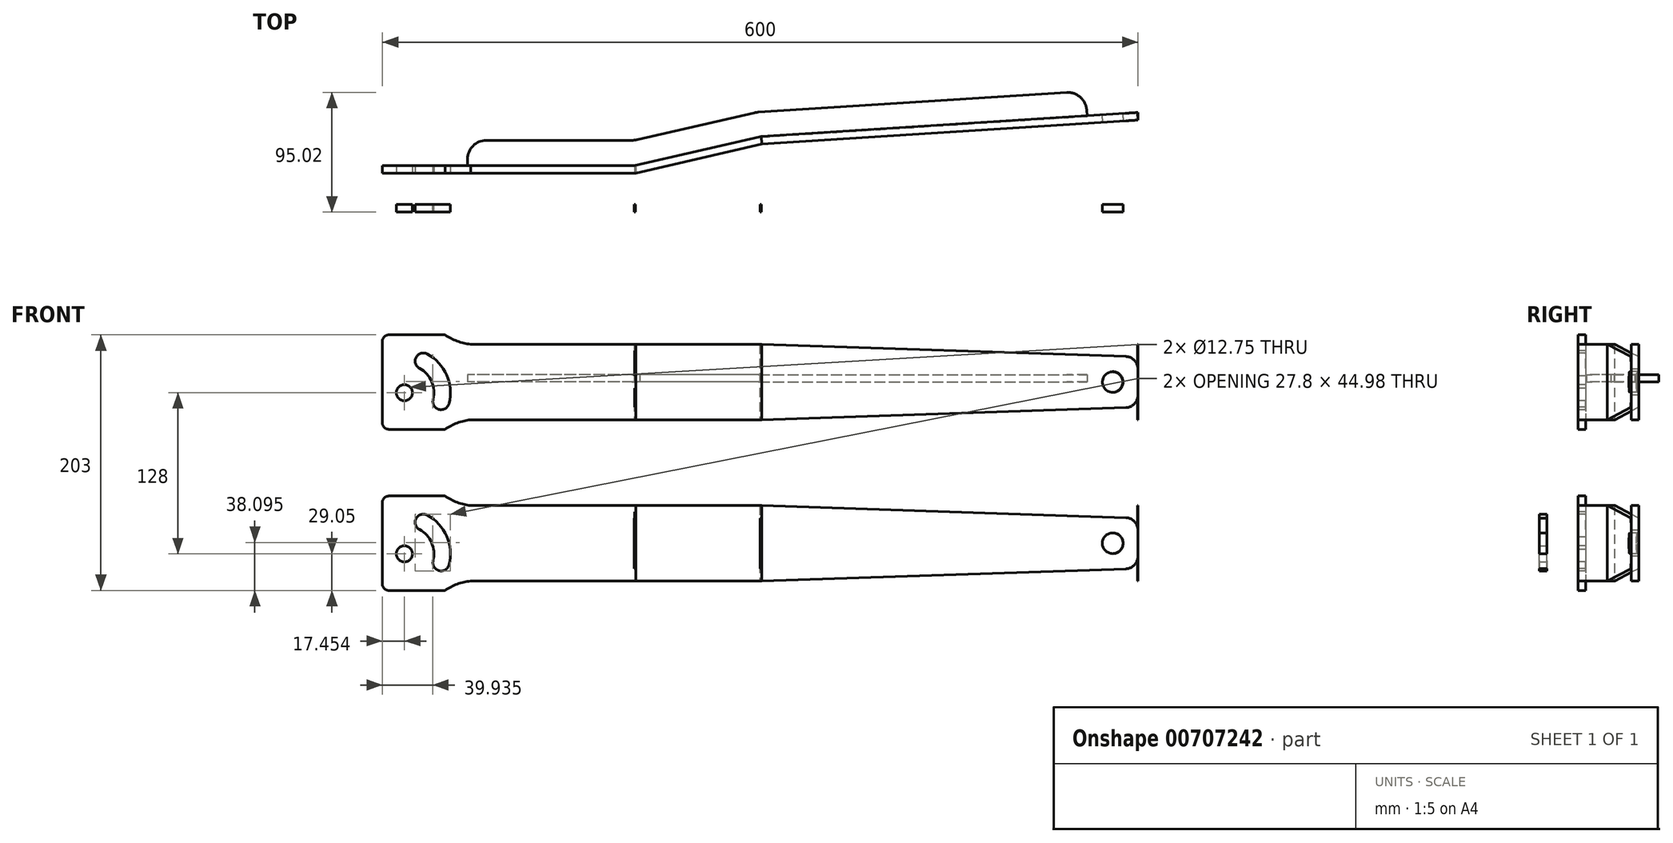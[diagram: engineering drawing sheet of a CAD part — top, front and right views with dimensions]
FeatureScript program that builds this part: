
annotation { "Feature Type Name" : "Feature", "Feature Type Description" : "" }
export const myFeature = defineFeature(function(context is Context, id is Id, definition is map)
    precondition{}
    {
        {
            var Q0;
            Q0=qCreatedBy(makeId("Top.planeOp"),FACE);
            var sketch = newSketch(context, id + "F0", { "sketchPlane" : qUnion([Q0])});
            skLineSegment(sketch, "E0", {"start": v(-300, 0) * mm, "end": v(300, 0) * mm, "construction": true});
            skLineSegment(sketch, "E1", {"start": v(-300, 0) * mm, "end": v(-100, 0) * mm});
            skLineSegment(sketch, "E2", {"start": v(-100, 0) * mm, "end": v(-0.38, 22.9) * mm});
            skLineSegment(sketch, "E3", {"start": v(-0.38, 22.9) * mm, "end": v(300, 42.09) * mm});
            skLineSegment(sketch, "E4", {"start": v(-300, 0) * mm, "end": v(-300, 128) * mm, "construction": true});
            skLineSegment(sketch, "E5.0", {"start": v(1.37, 17) * mm, "end": v(300, 36.07) * mm});
            skLineSegment(sketch, "E5.1", {"start": v(-98.63, -6) * mm, "end": v(1.37, 17) * mm});
            skLineSegment(sketch, "E5.2", {"start": v(-300, -6) * mm, "end": v(-98.63, -6) * mm});
            skLineSegment(sketch, "E6", {"start": v(-300, 0) * mm, "end": v(-300, -6) * mm});
            skLineSegment(sketch, "E7", {"start": v(300, 42.09) * mm, "end": v(300, 36.07) * mm});
            skLineSegment(sketch, "E8", {"start": v(-300, 33.9) * mm, "end": v(-300, 101.04) * mm});
            skLineSegment(sketch, "E9", {"start": v(-0.38, 22.9) * mm, "end": v(1.37, 17) * mm});
            skLineSegment(sketch, "E10", {"start": v(-100, 0) * mm, "end": v(-98.63, -6) * mm});
            skSolve(sketch);
        }
        {
            var Q0;
            Q0=qSketchRegion(id+"F0",true);
            extrude(context, id + "F1", {"entities" : qUnion([Q0]), "depth" : 60 * mm, "offsetDistance" : 25 * mm});
        }
        {
            var Q0;
            Q0=makeQuery(id+"F1.opExtrude","SWEPT_FACE",FACE,{"disambiguationData":[OSD([sQuery(id+"F0.wireOp",EDGE,"E5.2")])]});
            var sketch = newSketch(context, id + "F2", { "sketchPlane" : qUnion([Q0])});
            skLineSegment(sketch, "E11", {"start": v(-295, 67.5) * mm, "end": v(-250.3, 67.5) * mm});
            skPoint(sketch, "E12.visualSharp", {"position": v(-225, 67.5) * mm});
            skPoint(sketch, "E13.visualSharp", {"position": v(-225, -7.5) * mm});
            skPoint(sketch, "E14.visualSharp", {"position": v(-306, 67.5) * mm});
            skPoint(sketch, "E15.visualSharp", {"position": v(-300, -7.5) * mm});
            skPoint(sketch, "E16", {"position": v(-230, 60) * mm});
            skArc(sketch, "E17", {"start": v(-250.3, 67.5) * mm, "mid": v(-240.6, 62.51) * mm, "end": v(-230, 60) * mm});
            skPoint(sketch, "E18", {"position": v(-230, 0) * mm});
            skLineSegment(sketch, "E19", {"start": v(-230, 60) * mm, "end": v(-230, 0) * mm});
            skLineSegment(sketch, "E20", {"start": v(-98.63, 30) * mm, "end": v(-98.63, 30) * mm});
            skPoint(sketch, "E21.newPointA", {"position": v(-300, 67.5) * mm});
            skPoint(sketch, "E21.newPointB", {"position": v(-315.3, 67.5) * mm});
            skArc(sketch, "E21.filletArc", {"start": v(-295, 67.5) * mm, "mid": v(-298.54, 66.04) * mm, "end": v(-300, 62.5) * mm});
            skLineSegment(sketch, "E22", {"start": v(-240.6, 62.51) * mm, "end": v(-240.6, 0) * mm, "construction": true});
            skLineSegment(sketch, "E23.0", {"start": v(-300, 60) * mm, "end": v(-300, 0) * mm});
            skLineSegment(sketch, "E24", {"start": v(-300, 60) * mm, "end": v(-300, 62.5) * mm});
            skLineSegment(sketch, "E25", {"start": v(-300, 30) * mm, "end": v(-187.15, 30) * mm, "construction": true});
            skLineSegment(sketch, "E26.MirrorCS", {"start": v(-295, -7.5) * mm, "end": v(-250.3, -7.5) * mm});
            skArc(sketch, "E27.MirrorCS", {"start": v(-250.3, -7.5) * mm, "mid": v(-240.6, -2.51) * mm, "end": v(-230, 0) * mm});
            skArc(sketch, "E28.MirrorCS", {"start": v(-295, -7.5) * mm, "mid": v(-298.54, -6.04) * mm, "end": v(-300, -2.5) * mm});
            skLineSegment(sketch, "E29.MirrorCS", {"start": v(-300, 0) * mm, "end": v(-300, -2.5) * mm});
            skSolve(sketch);
        }
        {
            var Q0;
            Q0=makeQuery(id+"F1.opExtrude","SWEPT_FACE",FACE,{"disambiguationData":[OSD([sQuery(id+"F0.wireOp",EDGE,"E5.0")])]});
            var sketch = newSketch(context, id + "F3", { "sketchPlane" : qUnion([Q0])});
            skCircle(sketch, "E30", {"center": v(281.69, 30) * mm, "radius": 8.25 * mm});
            skPoint(sketch, "E30.centerSnap0", {"position": v(302.28, 30) * mm});
            skLineSegment(sketch, "E31", {"start": v(2.45, 60) * mm, "end": v(292.02, 50.32) * mm});
            skLineSegment(sketch, "E32", {"start": v(2.45, 0) * mm, "end": v(292.02, 9.68) * mm});
            skLineSegment(sketch, "E33", {"start": v(301.69, 40.33) * mm, "end": v(301.69, 19.67) * mm});
            skPoint(sketch, "E34.visualSharp", {"position": v(301.69, 50) * mm});
            skArc(sketch, "E34.filletArc", {"start": v(301.69, 40.33) * mm, "mid": v(298.88, 47.28) * mm, "end": v(292.02, 50.32) * mm});
            skPoint(sketch, "E35.visualSharp", {"position": v(301.69, 10) * mm});
            skArc(sketch, "E35.filletArc", {"start": v(292.02, 9.68) * mm, "mid": v(298.88, 12.72) * mm, "end": v(301.69, 19.67) * mm});
            skSolve(sketch);
        }
        {
            var Q0;
            {var subQ0=sQuery(id+"F3.wireOp",EDGE,"E31");Q0=makeQuery(id+"F3.imprint","IMPRINT",FACE,{"disambiguationData":[TD([[makeQuery(id+"F3.imprint","IMPRINT",EDGE,{"derivedFrom":subQ0}),1.0]])]});}
            var Q1;
            {var subQ0=sQuery(id+"F3.wireOp",EDGE,"E32");Q1=makeQuery(id+"F3.imprint","IMPRINT",FACE,{"disambiguationData":[TD([[makeQuery(id+"F3.imprint","IMPRINT",EDGE,{"derivedFrom":subQ0}),-1.0]])]});}
            var Q2;
            Q2=makeQuery(id+"F3.imprint","IMPRINT",FACE,{"disambiguationData":[TD([[makeQuery(id+"F3.imprint","IMPRINT",EDGE,{"derivedFrom":sQuery(id+"F3.wireOp",EDGE,"E30")}),1.0]])]});
            extrude(context, id + "F4", {"entities" : qUnion([Q0, Q1, Q2]), "operationType" : NewBodyOperationType.REMOVE, "oppositeDirection" : true, "depth" : 25 * mm, "offsetDistance" : 25 * mm});
        }
        {
            var Q0;
            Q0=makeQuery(id+"F2.imprint","IMPRINT",FACE,{"disambiguationData":[TD([[makeQuery(id+"F2.imprint","IMPRINT",EDGE,{"derivedFrom":sQuery(id+"F2.wireOp",EDGE,"E11")}),-1.0]])]});
            var Q1;
            Q1=makeQuery(id+"F2.imprint","IMPRINT",FACE,{"disambiguationData":[TD([[makeQuery(id+"F2.imprint","IMPRINT",EDGE,{"derivedFrom":sQuery(id+"F2.wireOp",EDGE,"6MBA5zCG-kA5Y-AlUf-X3c2-cWm0OstjSN9L")}),1.0]])]});
            extrude(context, id + "F5", {"entities" : qUnion([Q0, Q1]), "operationType" : NewBodyOperationType.ADD, "oppositeDirection" : true, "depth" : 6 * mm, "offsetDistance" : 25 * mm});
        }
        {
            var Q0;
            {var subQ0=sQuery(id+"F0.wireOp",EDGE,"E5.2");Q0=makeQuery(id+"F5.boolean.opBoolean","MERGE",FACE,{"derivedFrom":[makeQuery(id+"F1.opExtrude","SWEPT_FACE",FACE,{"disambiguationData":[OSD([subQ0])]}),makeQuery(id+"F5.opExtrude","CAP_FACE",FACE,{"disambiguationData":[OSD([subQ0,sQuery(id+"F2.wireOp",EDGE,"2KIgmFb8-dbBe-8aPb-DhG4-cKlgFUq4y2h1"),sQuery(id+"F2.wireOp",EDGE,"6MBA5zCG-kA5Y-AlUf-X3c2-cWm0OstjSN9L"),sQuery(id+"F2.wireOp",EDGE,"E15.filletArc"),sQuery(id+"F2.wireOp",EDGE,"07031323-947f-4b0b-b8ee-12b4b9ee6c110.MirrorCS")])],"isStart":true}),makeQuery(id+"F5.opExtrude","CAP_FACE",FACE,{"disambiguationData":[OSD([subQ0,sQuery(id+"F2.wireOp",EDGE,"E11"),sQuery(id+"F2.wireOp",EDGE,"E17"),sQuery(id+"F2.wireOp",EDGE,"2cHqhizW-JMVK-h9AF-USdZ-6RG1NBp1Brja"),sQuery(id+"F2.wireOp",EDGE,"E21.filletArc")])],"isStart":true})]});}
            var sketch = newSketch(context, id + "F6", { "sketchPlane" : qUnion([Q0])});
            skPoint(sketch, "E36.centerSnap0", {"position": v(-303.27, 27.75) * mm});
            skPoint(sketch, "E36.centerSnap1", {"position": v(-270.79, 64.03) * mm});
            skLineSegment(sketch, "E37", {"start": v(-271.04, 55.82) * mm, "end": v(-250.9, 3.47) * mm, "construction": true});
            skPoint(sketch, "E38.orphan", {"position": v(-256.1, 1.25) * mm});
            skLineSegment(sketch, "E39", {"start": v(-289.53, 18.87) * mm, "end": v(-224.13, 44.01) * mm, "construction": true});
            skPoint(sketch, "E40.center.orphan", {"position": v(-270.79, 26.53) * mm});
            skPoint(sketch, "E41.0.endCap.center.orphan", {"position": v(-269.46, 51.72) * mm});
            skPoint(sketch, "E41.0.left.start.orphan", {"position": v(-253.42, 14.54) * mm});
            skPoint(sketch, "E41.0.startCap.center.orphan", {"position": v(-252.07, 6.49) * mm});
            skPoint(sketch, "E42", {"position": v(-267.5, 46.62) * mm});
            skPoint(sketch, "E43", {"position": v(-256.25, 17.37) * mm});
            skArc(sketch, "E44", {"start": v(-253.42, 14.54) * mm, "mid": v(-254.95, 33) * mm, "end": v(-267.5, 46.62) * mm});
            skArc(sketch, "E45.0.startCap", {"start": v(-247.12, 12.94) * mm, "mid": v(-255.02, 8.24) * mm, "end": v(-259.72, 16.13) * mm});
            skArc(sketch, "E45.0.endCap", {"start": v(-270.59, 40.9) * mm, "mid": v(-273.22, 49.7) * mm, "end": v(-264.41, 52.34) * mm});
            skArc(sketch, "E45.0.left", {"start": v(-259.72, 16.13) * mm, "mid": v(-260.9, 30.39) * mm, "end": v(-270.59, 40.9) * mm});
            skArc(sketch, "E45.0.right", {"start": v(-247.12, 12.94) * mm, "mid": v(-249, 35.6) * mm, "end": v(-264.41, 52.34) * mm});
            skCircle(sketch, "E46", {"center": v(-282.55, 21.55) * mm, "radius": 6.38 * mm});
            skSolve(sketch);
        }
        {
            var Q0;
            Q0=qSketchRegion(id+"F6",true);
            extrude(context, id + "F7", {"entities" : qUnion([Q0]), "operationType" : NewBodyOperationType.REMOVE, "oppositeDirection" : true, "depth" : 25 * mm, "offsetDistance" : 25 * mm});
        }
        {
            var Q0;
            Q0=makeQuery(id+"F1.opExtrude","SWEPT_EDGE",EDGE,{"disambiguationData":[OSD([sQuery(id+"F0.wireOp",EDGE,"E1"),sQuery(id+"F0.wireOp",EDGE,"E2"),sQuery(id+"F0.wireOp",EDGE,"E10")])]});
            cPoint(context, id + "F8", {"entities" : qUnion([Q0]), "parameter" : 0.5});
        }
        {
            var Q0;
            Q0=makeQuery(id+"F1.opExtrude","SWEPT_EDGE",EDGE,{"disambiguationData":[OSD([sQuery(id+"F0.wireOp",EDGE,"E2"),sQuery(id+"F0.wireOp",EDGE,"E3"),sQuery(id+"F0.wireOp",EDGE,"E9")])]});
            cPoint(context, id + "F9", {"entities" : qUnion([Q0]), "parameter" : 0.5});
        }
        {
            var Q0;
            Q0=makeQuery(id+"F1.opExtrude","SWEPT_EDGE",EDGE,{"disambiguationData":[OSD([sQuery(id+"F0.wireOp",EDGE,"E3"),sQuery(id+"F0.wireOp",EDGE,"E7")])]});
            cPoint(context, id + "F10", {"entities" : qUnion([Q0]), "parameter" : 0.5});
        }
        {
            var Q0;
            Q0 = qCreatedBy(id + "F8" ,VERTEX);
            var Q1;
            Q1 = qCreatedBy(id + "F9" ,VERTEX);
            var Q2;
            Q2 = qCreatedBy(id + "F10" ,VERTEX);
            cPlane(context, id + "F11", {"entities" : qUnion([Q0, Q1, Q2]), "cplaneType" : CPlaneType.THREE_POINT, "offset" : 33 * mm, "oppositeDirection" : true, "width" : 150 * mm, "height" : 150 * mm});
        }
        {
            var Q0;
            Q0=qSketchRegion(id+"F2",true);
            extrude(context, id + "F13", {"entities" : qUnion([Q0]), "operationType" : NewBodyOperationType.ADD, "oppositeDirection" : true, "depth" : 6 * mm, "offsetDistance" : 25 * mm});
        }
        {
            var Q0;
            Q0=qSketchRegion(id+"F6",true);
            extrude(context, id + "F14", {"entities" : qUnion([Q0]), "operationType" : NewBodyOperationType.REMOVE, "oppositeDirection" : true, "depth" : 25 * mm, "offsetDistance" : 25 * mm});
        }
        {
            var Q0;
            Q0=qSketchRegion(id+"F6",true);
            extrude(context, id + "F15", {"entities" : qUnion([Q0]), "operationType" : NewBodyOperationType.REMOVE, "oppositeDirection" : true, "depth" : 25 * mm, "offsetDistance" : 25 * mm});
        }
        {
            var Q0;
            {var subQ0=sQuery(id+"F2.wireOp",EDGE,"E19");Q0=makeQuery(id+"F2.imprint","IMPRINT",FACE,{"disambiguationData":[TD([[makeQuery(id+"F2.imprint","IMPRINT",EDGE,{"derivedFrom":subQ0}),1.0]])]});}
            var sketch = newSketch(context, id + "F16", { "sketchPlane" : qUnion([Q0])});
            skLineSegment(sketch, "E47.0", {"start": v(-98.63, 55) * mm, "end": v(-98.63, 35) * mm});
            skLineSegment(sketch, "E48", {"start": v(-150.92, 10) * mm, "end": v(-146.58, 10) * mm, "construction": true});
            skLineSegment(sketch, "E49", {"start": v(-146.58, 30) * mm, "end": v(-98.63, 30) * mm, "construction": true});
            skLineSegment(sketch, "E50", {"start": v(-143.51, 35) * mm, "end": v(-98.63, 35) * mm, "construction": true});
            skLineSegment(sketch, "E51", {"start": v(-147.72, 25) * mm, "end": v(-151.64, 25) * mm, "construction": true});
            skPoint(sketch, "E52.orphan", {"position": v(-98.63, 60) * mm});
            skLineSegment(sketch, "E53.trimOffspring", {"start": v(-98.63, 25) * mm, "end": v(-98.63, 10) * mm});
            skPoint(sketch, "E54.orphan", {"position": v(-98.63, 0) * mm});
            skLineSegment(sketch, "E55.0", {"start": v(-99.63, 25) * mm, "end": v(-99.63, 10) * mm});
            skLineSegment(sketch, "E56.0", {"start": v(-99.63, 55) * mm, "end": v(-99.63, 35) * mm});
            skLineSegment(sketch, "E57", {"start": v(-99.63, 35) * mm, "end": v(-98.63, 35) * mm});
            skLineSegment(sketch, "E58", {"start": v(-99.63, 55) * mm, "end": v(-98.63, 55) * mm});
            skLineSegment(sketch, "E59", {"start": v(-99.63, 10) * mm, "end": v(-98.63, 10) * mm});
            skLineSegment(sketch, "E60", {"start": v(-99.63, 25) * mm, "end": v(-98.63, 25) * mm});
            skPoint(sketch, "E61.end.orphan", {"position": v(-146.58, 55) * mm});
            skSolve(sketch);
        }
        {
            var Q0;
            Q0=qSketchRegion(id+"F16",true);
            extrude(context, id + "F17", {"entities" : qUnion([Q0]), "operationType" : NewBodyOperationType.REMOVE, "oppositeDirection" : true, "depth" : 25 * mm, "offsetDistance" : 25 * mm});
        }
        {
            var Q0;
            Q0=makeQuery(id+"F1.opExtrude","SWEPT_BODY",BODY,{"disambiguationData":[OSD([sQuery(id+"F0.wireOp",EDGE,"E1"),sQuery(id+"F0.wireOp",EDGE,"E2"),sQuery(id+"F0.wireOp",EDGE,"E3"),sQuery(id+"F0.wireOp",EDGE,"E5.0"),sQuery(id+"F0.wireOp",EDGE,"E5.1"),sQuery(id+"F0.wireOp",EDGE,"E5.2"),sQuery(id+"F0.wireOp",EDGE,"E6"),sQuery(id+"F0.wireOp",EDGE,"E7")])]});
            transform(context, id + "F18", {"entities" : qUnion([Q0]), "transformType" : TransformType.TRANSLATION_3D, "dx" : 0 * mm, "dy" : 0 * mm, "dz" : -128 * mm, "makeCopy" : true});
        }
        {
            var Q0;
            {var subQ0=sQuery(id+"F2.wireOp",EDGE,"E24");var subQ1=sQuery(id+"F2.wireOp",EDGE,"E21.filletArc");var subQ2=sQuery(id+"F2.wireOp",EDGE,"E17");var subQ3=sQuery(id+"F2.wireOp",EDGE,"E11");var subQ4=sQuery(id+"F0.wireOp",EDGE,"E5.2");Q0=makeQuery(id+"F18.opPattern","COPY",FACE,{"derivedFrom":makeQuery(id+"F13.boolean.opBoolean","MERGE",FACE,{"derivedFrom":[makeQuery(id+"F5.boolean.opBoolean","MERGE",FACE,{"derivedFrom":[makeQuery(id+"F1.opExtrude","SWEPT_FACE",FACE,{"disambiguationData":[OSD([subQ4])]}),makeQuery(id+"F5.opExtrude","CAP_FACE",FACE,{"disambiguationData":[OSD([subQ4,subQ3,subQ2,subQ1,subQ0])],"isStart":true})]}),makeQuery(id+"F13.opExtrude","CAP_FACE",FACE,{"disambiguationData":[OSD([subQ3,subQ2,sQuery(id+"F2.wireOp",EDGE,"E19"),subQ1,sQuery(id+"F2.wireOp",EDGE,"E23.0"),subQ0,sQuery(id+"F2.wireOp",EDGE,"E26.MirrorCS"),sQuery(id+"F2.wireOp",EDGE,"E27.MirrorCS"),sQuery(id+"F2.wireOp",EDGE,"E28.MirrorCS"),sQuery(id+"F2.wireOp",EDGE,"E29.MirrorCS")])],"isStart":true})]}),"instanceName":"1"});}
            cPlane(context, id + "F19", {"entities" : qUnion([Q0]), "cplaneType" : CPlaneType.OFFSET, "offset" : 25 * mm, "width" : 150 * mm, "height" : 150 * mm});
        }
        {
            var Q0;
            Q0=qCreatedBy(id+"F19.planeOp",FACE);
            var sketch = newSketch(context, id + "F20", { "sketchPlane" : qUnion([Q0])});
            skLineSegment(sketch, "E62.0.3", {"start": v(-98.63, -68) * mm, "end": v(-230, -68) * mm});
            skArc(sketch, "E62.0.4", {"start": v(-230, -68) * mm, "mid": v(-240.6, -65.49) * mm, "end": v(-250.3, -60.5) * mm});
            skLineSegment(sketch, "E62.0.5", {"start": v(-250.3, -60.5) * mm, "end": v(-295, -60.5) * mm});
            skArc(sketch, "E62.0.6", {"start": v(-295, -60.5) * mm, "mid": v(-298.54, -61.96) * mm, "end": v(-300, -65.5) * mm});
            skLineSegment(sketch, "E62.0.7", {"start": v(-300, -65.5) * mm, "end": v(-300, -130.5) * mm});
            skArc(sketch, "E62.0.8", {"start": v(-300, -130.5) * mm, "mid": v(-298.54, -134.04) * mm, "end": v(-295, -135.5) * mm});
            skLineSegment(sketch, "E62.0.9", {"start": v(-295, -135.5) * mm, "end": v(-250.3, -135.5) * mm});
            skArc(sketch, "E62.0.10", {"start": v(-250.3, -135.5) * mm, "mid": v(-240.6, -130.51) * mm, "end": v(-230, -128) * mm});
            skLineSegment(sketch, "E62.0.11", {"start": v(-230, -128) * mm, "end": v(-98.63, -128) * mm});
            skCircle(sketch, "E63.0", {"center": v(-282.55, -106.45) * mm, "radius": 6.38 * mm});
            skArc(sketch, "E64.0", {"start": v(-259.72, -111.87) * mm, "mid": v(-260.9, -97.61) * mm, "end": v(-270.59, -87.1) * mm});
            skArc(sketch, "E65.0", {"start": v(-270.59, -87.1) * mm, "mid": v(-273.22, -78.3) * mm, "end": v(-264.41, -75.66) * mm});
            skArc(sketch, "E66.0", {"start": v(-247.12, -115.06) * mm, "mid": v(-249, -92.4) * mm, "end": v(-264.41, -75.66) * mm});
            skArc(sketch, "E67.0", {"start": v(-247.12, -115.06) * mm, "mid": v(-255.02, -119.76) * mm, "end": v(-259.72, -111.87) * mm});
            skLineSegment(sketch, "E68.0", {"start": v(-98.63, -68) * mm, "end": v(1.37, -68) * mm});
            skLineSegment(sketch, "E69.0", {"start": v(-98.63, -128) * mm, "end": v(1.37, -128) * mm});
            skLineSegment(sketch, "E70.0", {"start": v(1.37, -68) * mm, "end": v(290.35, -77.68) * mm});
            skLineSegment(sketch, "E71.0", {"start": v(1.37, -128) * mm, "end": v(290.35, -118.32) * mm});
            skCircle(sketch, "E72.0", {"center": v(280, -98) * mm, "radius": 8.25 * mm});
            skArc(sketch, "E73.0", {"start": v(300, -87.67) * mm, "mid": v(297.19, -80.72) * mm, "end": v(290.33, -77.68) * mm});
            skArc(sketch, "E74.0", {"start": v(290.33, -118.32) * mm, "mid": v(297.19, -115.28) * mm, "end": v(300, -108.33) * mm});
            skLineSegment(sketch, "E75.0", {"start": v(300, -87.67) * mm, "end": v(300, -108.33) * mm});
            skLineSegment(sketch, "E76", {"start": v(-99, -118) * mm, "end": v(1, -118) * mm, "construction": true});
            skLineSegment(sketch, "E77", {"start": v(-100, -78) * mm, "end": v(0, -78) * mm, "construction": true});
            skLineSegment(sketch, "E78.bottom", {"start": v(-100, -78) * mm, "end": v(-99, -78) * mm});
            skLineSegment(sketch, "E78.top", {"start": v(-100, -118) * mm, "end": v(-99, -118) * mm});
            skLineSegment(sketch, "E78.left", {"start": v(-100, -78) * mm, "end": v(-100, -118) * mm});
            skLineSegment(sketch, "E78.right", {"start": v(-99, -118) * mm, "end": v(-99, -78) * mm});
            skLineSegment(sketch, "E79.bottom", {"start": v(0, -78) * mm, "end": v(1, -78) * mm});
            skLineSegment(sketch, "E79.top", {"start": v(0, -118) * mm, "end": v(1, -118) * mm});
            skLineSegment(sketch, "E79.left", {"start": v(0, -78) * mm, "end": v(0, -118) * mm});
            skLineSegment(sketch, "E79.right", {"start": v(1, -118) * mm, "end": v(1, -78) * mm});
            skSolve(sketch);
        }
        {
            var Q0;
            Q0 = qSketchRegion(id + "F20", true);
            extrude(context, id + "F21", {"entities" : qUnion([Q0]), "depth" : 6 * mm, "offsetDistance" : 25 * mm});
        }
        {
            var Q0;
            Q0=qCreatedBy(id+"F11.planeOp",FACE);
            var sketch = newSketch(context, id + "F22", { "sketchPlane" : qUnion([Q0])});
            skLineSegment(sketch, "E80", {"start": v(0, 22.4) * mm, "end": v(259.62, 38.99) * mm});
            skLineSegment(sketch, "E81", {"start": v(0, 22.4) * mm, "end": v(-95.73, 0.4) * mm});
            skLineSegment(sketch, "E82", {"start": v(-100.78, 0) * mm, "end": v(-232.46, 0) * mm});
            skLineSegment(sketch, "E83.0", {"start": v(-1.27, 42.36) * mm, "end": v(243.41, 58) * mm});
            skLineSegment(sketch, "E83.1", {"start": v(-4.48, 41.9) * mm, "end": v(-97.52, 20.5) * mm});
            skLineSegment(sketch, "E83.2", {"start": v(-102, 20) * mm, "end": v(-217.46, 20) * mm});
            skLineSegment(sketch, "E84", {"start": v(259.62, 38.99) * mm, "end": v(259.34, 43.87) * mm});
            skLineSegment(sketch, "E85", {"start": v(-232.46, 0) * mm, "end": v(-232.46, 5) * mm});
            skPoint(sketch, "E86.visualSharp", {"position": v(258.49, 58.95) * mm});
            skArc(sketch, "E86.filletArc", {"start": v(259.34, 43.87) * mm, "mid": v(254.32, 54.25) * mm, "end": v(243.41, 58) * mm});
            skPoint(sketch, "E87.visualSharp", {"position": v(-232.46, 20) * mm});
            skArc(sketch, "E87.filletArc", {"start": v(-217.46, 20) * mm, "mid": v(-228.06, 15.6) * mm, "end": v(-232.46, 5) * mm});
            skPoint(sketch, "E88.visualSharp", {"position": v(-97.46, 0) * mm});
            skPoint(sketch, "E89.visualSharp", {"position": v(-99.73, 20) * mm});
            skArc(sketch, "E89.filletArc", {"start": v(-99.77, 20) * mm, "mid": v(-99.73, 20) * mm, "end": v(-99.68, 20.01) * mm});
            skArc(sketch, "E90.filletArc", {"start": v(-102, 20) * mm, "mid": v(-99.74, 20.13) * mm, "end": v(-97.52, 20.5) * mm});
            skLineSegment(sketch, "E91", {"start": v(-100.78, 0) * mm, "end": v(-100.13, 0) * mm});
            skLineSegment(sketch, "E92", {"start": v(-95.73, 0.4) * mm, "end": v(-100.13, 0) * mm});
            skPoint(sketch, "E93.visualSharp", {"position": v(-2.9, 42.26) * mm});
            skArc(sketch, "E93.filletArc", {"start": v(-1.27, 42.36) * mm, "mid": v(-2.89, 42.2) * mm, "end": v(-4.48, 41.9) * mm});
            skSolve(sketch);
        }
        {
            var Q0;
            Q0 = qSketchRegion(id + "F22", true);
            extrude(context, id + "F23", {"entities" : qUnion([Q0]), "depth" : 6 * mm, "offsetDistance" : 25 * mm});
        }
    });
